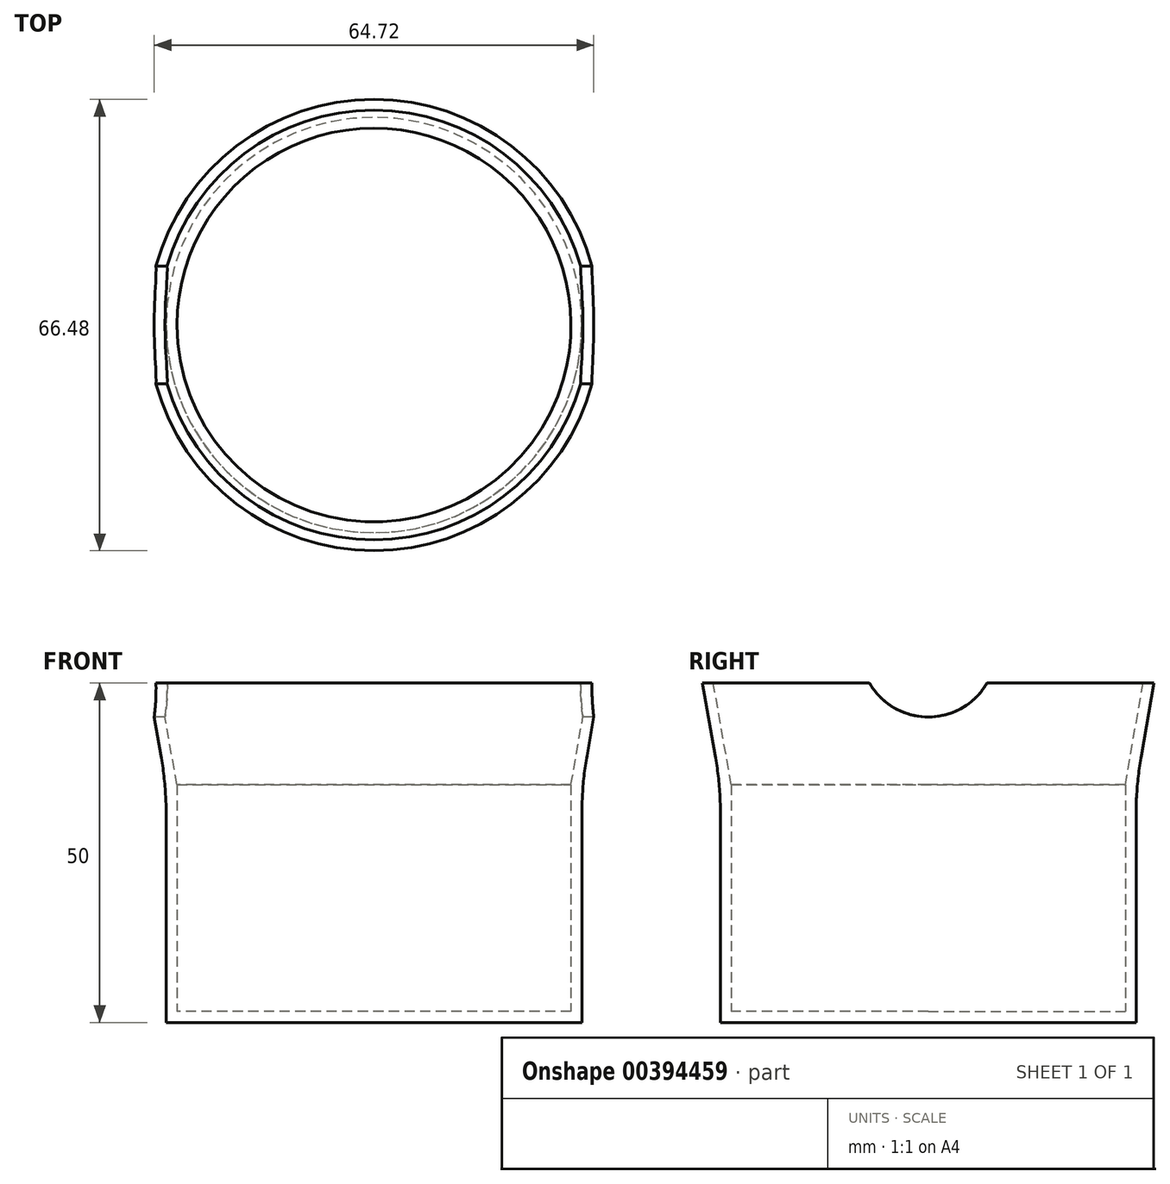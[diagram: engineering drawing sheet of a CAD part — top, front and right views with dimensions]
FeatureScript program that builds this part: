
annotation { "Feature Type Name" : "Feature", "Feature Type Description" : "" }
export const myFeature = defineFeature(function(context is Context, id is Id, definition is map)
    precondition{}
    {
        {
            var Q0;
            Q0=qCreatedBy(makeId("Top.planeOp"),FACE);
            var sketch = newSketch(context, id + "F0", { "sketchPlane" : qUnion([Q0])});
            skCircle(sketch, "E0", {"center": v(0, 0) * mm, "radius": 29 * mm});
            skCircle(sketch, "E1.0", {"center": v(0, 0) * mm, "radius": 30.6 * mm});
            skSolve(sketch);
        }
        {
            var Q0;
            Q0=makeQuery(id+"F0.imprint","IMPRINT",FACE,{"disambiguationData":[TD([[makeQuery(id+"F0.imprint","IMPRINT",EDGE,{"derivedFrom":sQuery(id+"F0.wireOp",EDGE,"E0")}),1.0]])]});
            extrude(context, id + "F1", {"entities" : qUnion([Q0]), "depth" : 1.6 * mm});
        }
        {
            var Q0;
            Q0 = qSketchRegion(id + "F0", true);
            extrude(context, id + "F2", {"entities" : qUnion([Q0]), "operationType" : NewBodyOperationType.ADD, "depth" : 35 * mm});
        }
        {
            var Q0;
            Q0=qCreatedBy(makeId("Front.planeOp"),FACE);
            var sketch = newSketch(context, id + "F3", { "sketchPlane" : qUnion([Q0])});
            skLineSegment(sketch, "E2", {"start": v(-31.36, 39.3) * mm, "end": v(-33.24, 50) * mm});
            skLineSegment(sketch, "E3", {"start": v(-33.24, 50) * mm, "end": v(-31.64, 50) * mm});
            skLineSegment(sketch, "E4", {"start": v(-31.64, 50) * mm, "end": v(-29, 35) * mm});
            skLineSegment(sketch, "E5", {"start": v(-30.6, 35) * mm, "end": v(-30.6, 30.63) * mm});
            skLineSegment(sketch, "E6", {"start": v(-30.6, 35) * mm, "end": v(-29, 35) * mm});
            skArc(sketch, "E7.filletArc", {"start": v(-30.6, 30.63) * mm, "mid": v(-30.8, 34.98) * mm, "end": v(-31.36, 39.3) * mm});
            skSolve(sketch);
        }
        {
            var Q0;
            Q0=makeQuery(id+"F3.imprint","IMPRINT",FACE,{"disambiguationData":[TD([[makeQuery(id+"F3.imprint","IMPRINT",EDGE,{"derivedFrom":sQuery(id+"F3.wireOp",EDGE,"E2")}),-1.0]])]});
            var Q1;
            Q1=makeQuery(id+"F2.opExtrude","CAP_EDGE",EDGE,{"disambiguationData":[OSD([sQuery(id+"F0.wireOp",EDGE,"E1.0")])],"isStart":false});
            sweep(context, id + "F4", {"operationType" : NewBodyOperationType.ADD, "profiles" : qUnion([Q0]), "path" : qUnion([Q1])});
        }
        {
            var Q0;
            Q0=qCreatedBy(makeId("Right.planeOp"),FACE);
            var sketch = newSketch(context, id + "F5", { "sketchPlane" : qUnion([Q0])});
            skCircle(sketch, "E8", {"center": v(0, 55) * mm, "radius": 10 * mm});
            skSolve(sketch);
        }
        {
            var Q0;
            Q0=makeQuery(id+"F5.imprint","IMPRINT",FACE,{"disambiguationData":[TD([[makeQuery(id+"F5.imprint","IMPRINT",EDGE,{"derivedFrom":sQuery(id+"F5.wireOp",EDGE,"E8")}),1.0]])]});
            extrude(context, id + "F6", {"entities" : qUnion([Q0]), "operationType" : NewBodyOperationType.REMOVE, "endBound" : BoundingType.SYMMETRIC, "depth" : 80 * mm});
        }
    });
